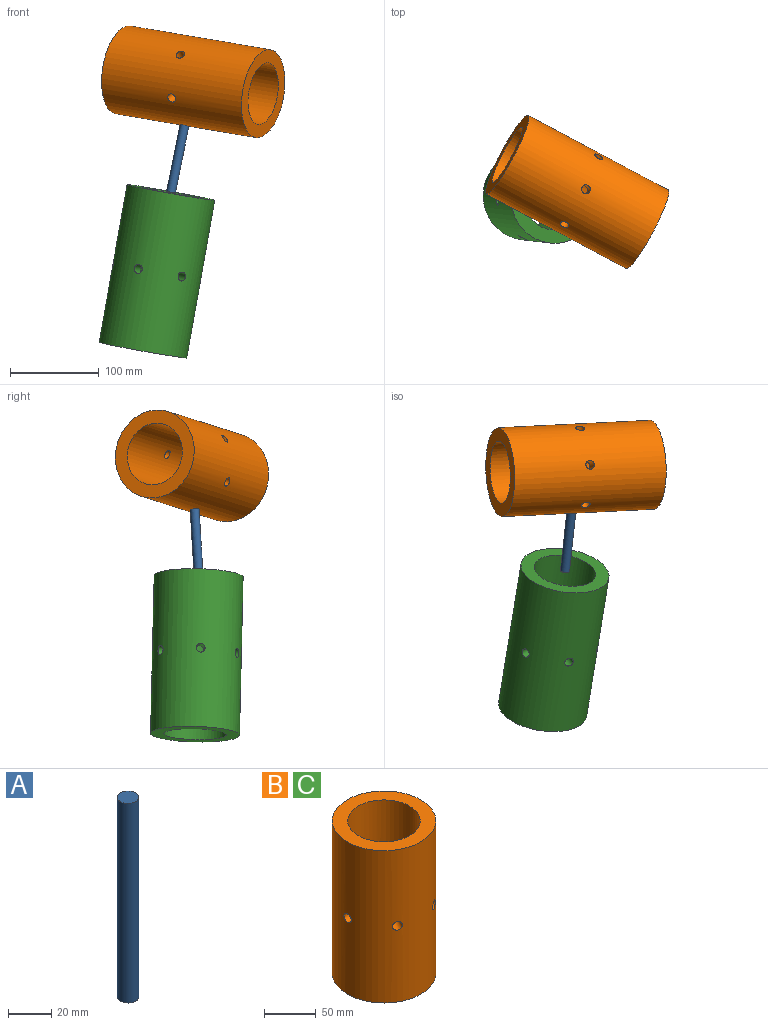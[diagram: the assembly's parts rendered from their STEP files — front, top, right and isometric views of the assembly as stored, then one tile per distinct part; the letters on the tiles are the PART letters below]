
ASSEMBLY  parts=3 mates=2
PART A: 3 faces, bbox 10x10x113.4 mm
  f0: cylinder r=5mm len=113.4mm, axis (0,0,-1), area 3562.6mm2, adj f1,f2
  f1: plane 10x10mm, normal (0,0,1), area 78.5mm2, adj f0
  f2: plane 10x10mm, normal (0,0,-1), area 78.5mm2, adj f0
PART B: 10 faces, bbox 100x100x180 mm
  f0: cylinder r=35mm len=180mm, axis (0,0,-1), area 39109.7mm2, adj f2,f3,f4,f5,f6,f7,f8,f9
  f1: cylinder r=50mm len=180mm, axis (0,0,-1), area 56075.5mm2, adj f2,f3,f4,f5,f6,f7,f8,f9
  f2: plane 100x100mm, normal (0,0,1), area 4005.5mm2, adj f0,f1
  f3: plane 100x100mm, normal (0,0,-1), area 4005.5mm2, adj f0,f1
  f4: cylinder r=5mm len=18.3mm, axis (-0.5,-0.87,0), area 472.9mm2, adj f0,f1
  f5: cylinder r=5mm len=15.36mm, axis (-1,0,0), area 472.9mm2, adj f0,f1
  f6: cylinder r=5mm len=18.3mm, axis (-0.5,0.87,0), area 472.9mm2, adj f0,f1
  f7: cylinder r=5mm len=15.36mm, axis (1,0,0), area 472.9mm2, adj f0,f1
  f8: cylinder r=5mm len=18.3mm, axis (-0.5,0.87,0), area 472.9mm2, adj f0,f1
  f9: cylinder r=5mm len=18.3mm, axis (0.5,0.87,0), area 472.9mm2, adj f0,f1
PART C: same geometry as B
PLACE A rot(axis=(-0.2,0.35,-0.92),29.8deg) t=(109.15,-53.93,84.69)mm
PLACE B rot(axis=(-0.63,0.21,0.75),165.1deg) t=(212.76,-88.23,195.82)mm
PLACE C rot(axis=(0.15,0.89,0.42),11.2deg) t=(77.73,-49.87,-92.5)mm fixed
MATE slider A.f0 <-> B.f5  axis (0.2,0.06,0.98) through (131.47,-47.23,195.67)mm
MATE ball C.f0 <-> A.f0  axis (-0.17,0.02,-0.98) through (109.15,-53.93,84.69)mm
